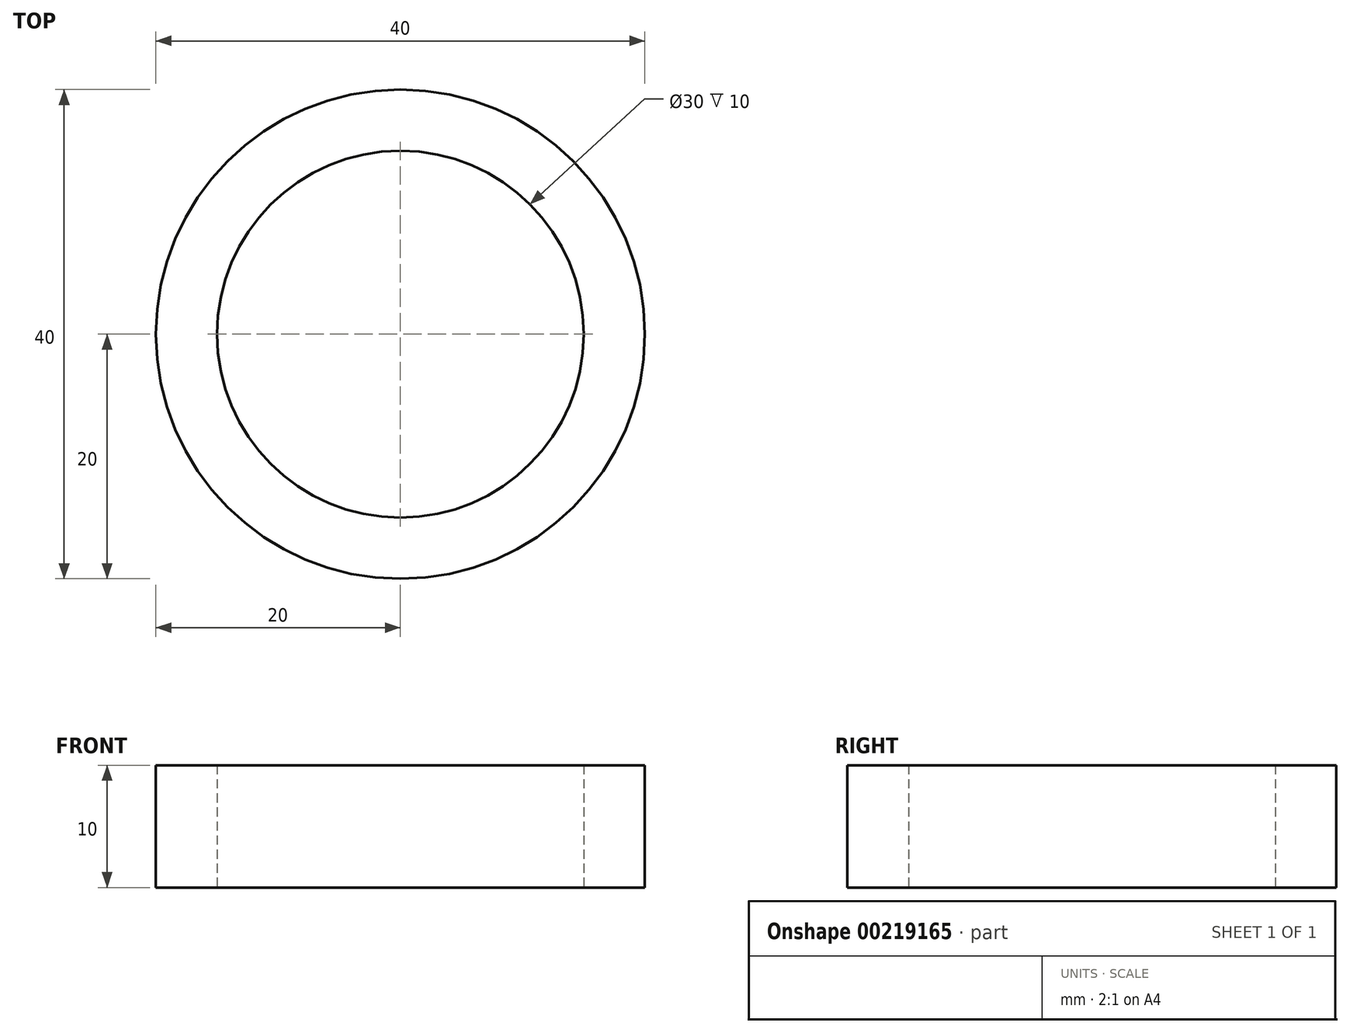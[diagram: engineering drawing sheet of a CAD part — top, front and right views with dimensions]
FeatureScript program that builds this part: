
annotation { "Feature Type Name" : "Feature", "Feature Type Description" : "" }
export const myFeature = defineFeature(function(context is Context, id is Id, definition is map)
    precondition{}
    {
        {
            var Q0;
            Q0=qCreatedBy(makeId("Top.planeOp"),FACE);
            var sketch = newSketch(context, id + "F0", { "sketchPlane" : qUnion([Q0])});
            skCircle(sketch, "E0", {"center": v(0, 0) * mm, "radius": 15 * mm});
            skCircle(sketch, "E1", {"center": v(0, 0) * mm, "radius": 20 * mm});
            skSolve(sketch);
        }
        {
            var Q0;
            Q0=makeQuery(id+"F0.imprint","IMPRINT",FACE,{"disambiguationData":[TD([[makeQuery(id+"F0.imprint","IMPRINT",EDGE,{"derivedFrom":sQuery(id+"F0.wireOp",EDGE,"E0")}),-1.0]])]});
            extrude(context, id + "F1", {"entities" : qUnion([Q0]), "depth" : 10 * mm});
        }
    });
